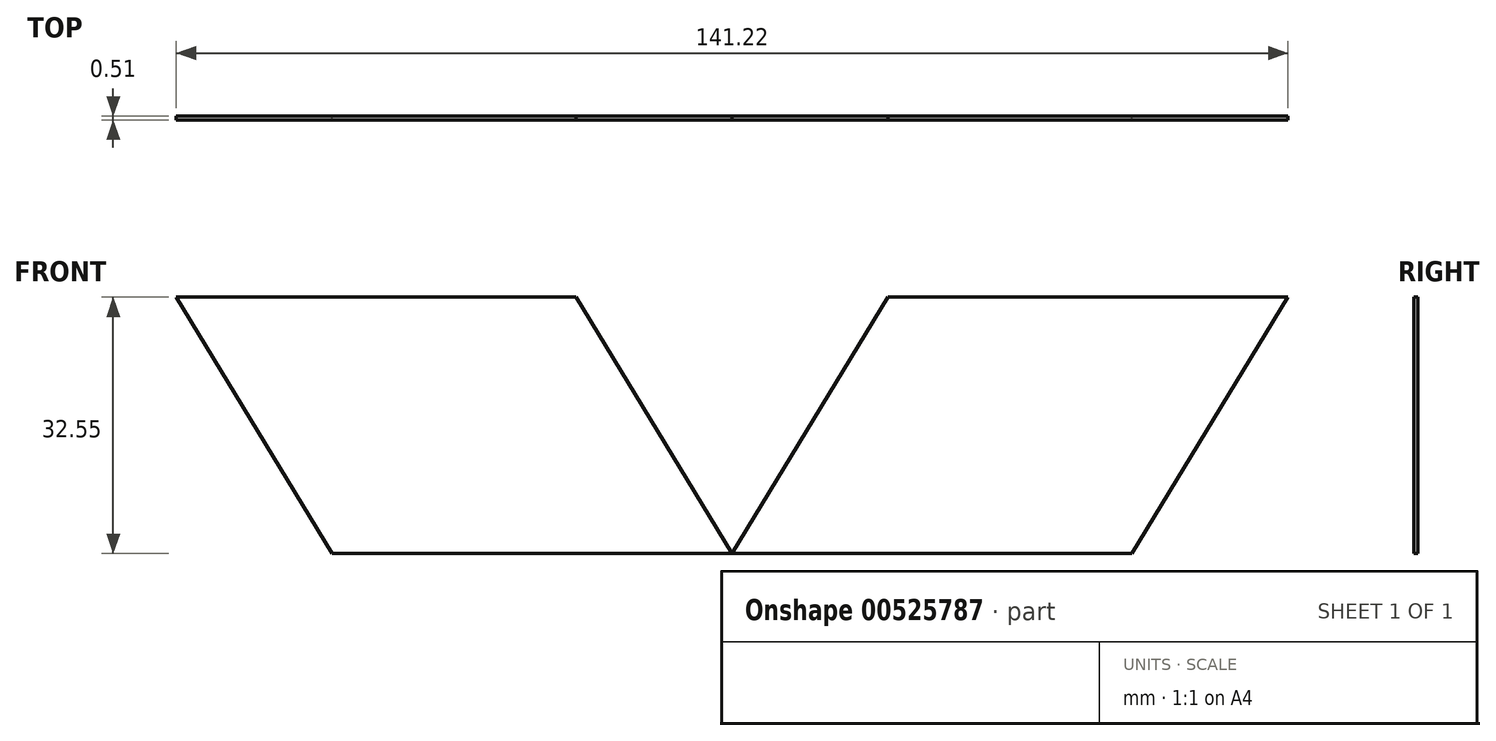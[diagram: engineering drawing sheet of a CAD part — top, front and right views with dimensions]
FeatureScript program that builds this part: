
annotation { "Feature Type Name" : "Feature", "Feature Type Description" : "" }
export const myFeature = defineFeature(function(context is Context, id is Id, definition is map)
    precondition{}
    {
        {
            var Q0;
            Q0=qCreatedBy(makeId("Front.planeOp"),FACE);
            var sketch = newSketch(context, id + "F0", { "sketchPlane" : qUnion([Q0])});
            skLineSegment(sketch, "E0", {"start": v(0, 0) * mm, "end": v(-50.8, 0) * mm});
            skLineSegment(sketch, "E1", {"start": v(-19.8, 32.55) * mm, "end": v(0, 0) * mm});
            skLineSegment(sketch, "E2", {"start": v(0, 0) * mm, "end": v(50.8, 0) * mm});
            skLineSegment(sketch, "E3", {"start": v(19.8, 32.55) * mm, "end": v(0, 0) * mm});
            skLineSegment(sketch, "E4", {"start": v(-19.8, 32.55) * mm, "end": v(-70.6, 32.55) * mm});
            skLineSegment(sketch, "E5", {"start": v(-70.6, 32.55) * mm, "end": v(-50.8, 0) * mm});
            skLineSegment(sketch, "E6", {"start": v(19.8, 32.55) * mm, "end": v(70.6, 32.55) * mm});
            skLineSegment(sketch, "E7", {"start": v(70.6, 32.55) * mm, "end": v(50.8, 0) * mm});
            skLineSegment(sketch, "E8", {"start": v(-19.8, 32.55) * mm, "end": v(-19.8, 0) * mm});
            skLineSegment(sketch, "E9", {"start": v(19.8, 32.55) * mm, "end": v(19.8, 0) * mm});
            skSolve(sketch);
        }
        {
            var Q0;
            Q0=makeQuery(id+"F0.imprint","IMPRINT",FACE,{"disambiguationData":[TD([[makeQuery(id+"F0.imprint","IMPRINT",EDGE,{"derivedFrom":sQuery(id+"F0.wireOp",EDGE,"E4")}),1.0]])]});
            var Q1;
            {var subQ0=sQuery(id+"F0.wireOp",EDGE,"E1");Q1=makeQuery(id+"F0.imprint","IMPRINT",FACE,{"disambiguationData":[TD([[makeQuery(id+"F0.imprint","IMPRINT",EDGE,{"derivedFrom":subQ0}),-1.0]])]});}
            var Q2;
            {var subQ0=sQuery(id+"F0.wireOp",EDGE,"E3");Q2=makeQuery(id+"F0.imprint","IMPRINT",FACE,{"disambiguationData":[TD([[makeQuery(id+"F0.imprint","IMPRINT",EDGE,{"derivedFrom":subQ0}),1.0]])]});}
            var Q3;
            Q3=makeQuery(id+"F0.imprint","IMPRINT",FACE,{"disambiguationData":[TD([[makeQuery(id+"F0.imprint","IMPRINT",EDGE,{"derivedFrom":sQuery(id+"F0.wireOp",EDGE,"E6")}),-1.0]])]});
            extrude(context, id + "F1", {"entities" : qUnion([Q0, Q1, Q2, Q3]), "depth" : 0.5 * mm, "offsetDistance" : 25.4 * mm});
        }
    });
